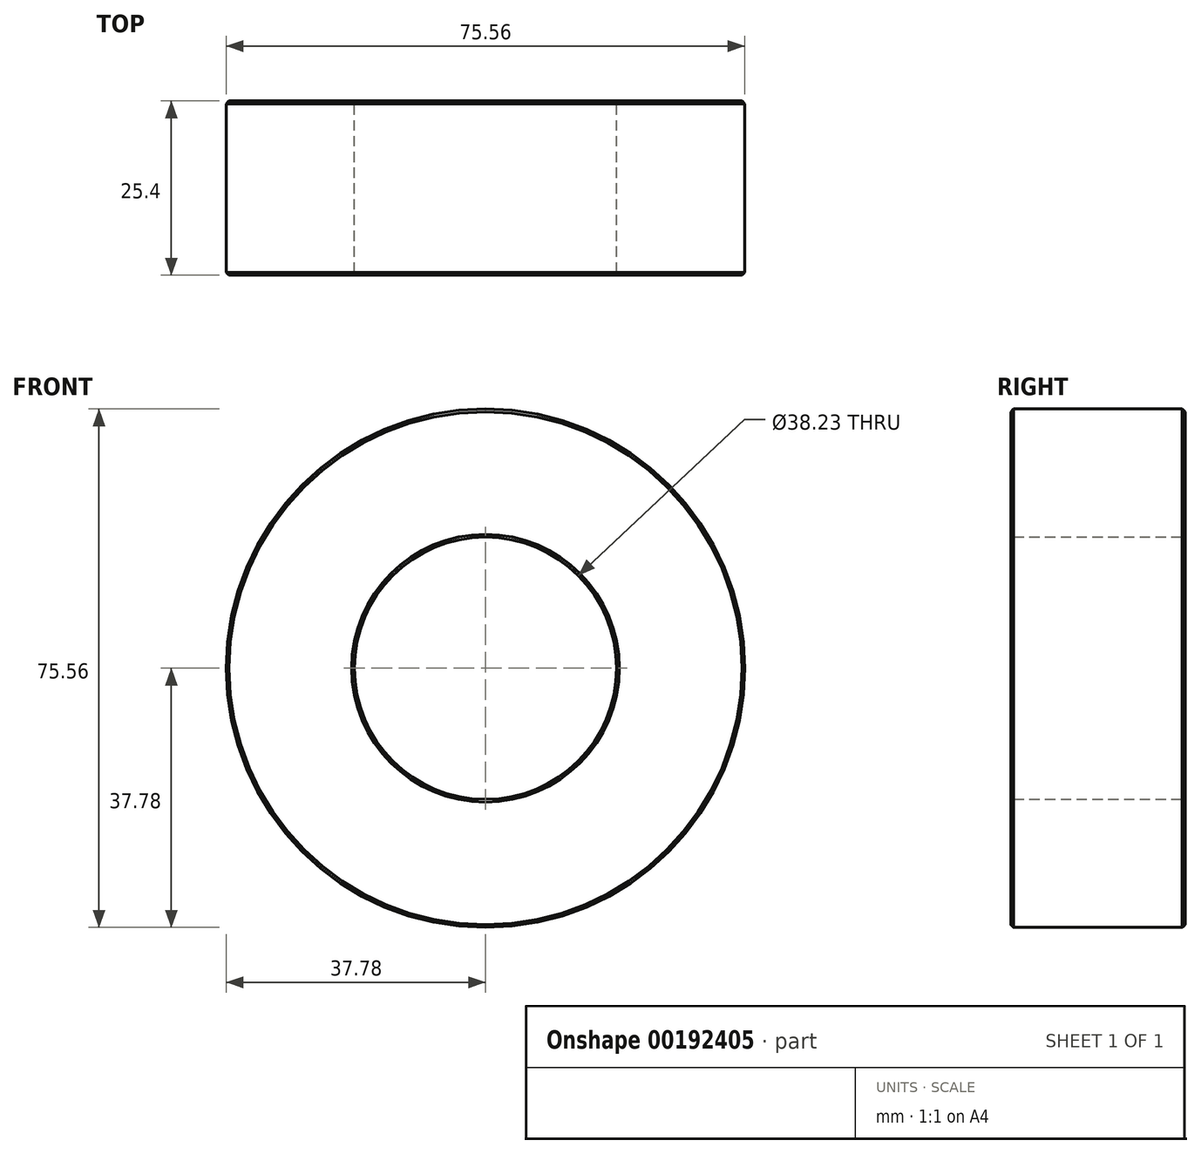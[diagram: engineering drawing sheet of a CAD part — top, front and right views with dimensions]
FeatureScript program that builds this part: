
annotation { "Feature Type Name" : "Feature", "Feature Type Description" : "" }
export const myFeature = defineFeature(function(context is Context, id is Id, definition is map)
    precondition{}
    {
        {
            var Q0;
            Q0=qCreatedBy(makeId("Front.planeOp"),FACE);
            var sketch = newSketch(context, id + "F0", { "sketchPlane" : qUnion([Q0])});
            skCircle(sketch, "E0", {"center": v(0, 0) * mm, "radius": 37.78 * mm});
            skCircle(sketch, "E1", {"center": v(0, 0) * mm, "radius": 19.11 * mm});
            skSolve(sketch);
        }
        {
            var Q0;
            Q0 = qSketchRegion(id + "F0", true);
            extrude(context, id + "F1", {"entities" : qUnion([Q0]), "depth" : 25.4 * mm});
        }
        {
            var Q0;
            Q0=makeQuery(id+"F1.opExtrude","CAP_EDGE",EDGE,{"disambiguationData":[OSD([sQuery(id+"F0.wireOp",EDGE,"E0")])],"isStart":false});
            var Q1;
            Q1=makeQuery(id+"F1.opExtrude","CAP_EDGE",EDGE,{"disambiguationData":[OSD([sQuery(id+"F0.wireOp",EDGE,"E1")])],"isStart":false});
            var Q2;
            Q2=makeQuery(id+"F1.opExtrude","CAP_EDGE",EDGE,{"disambiguationData":[OSD([sQuery(id+"F0.wireOp",EDGE,"E1")])],"isStart":true});
            var Q3;
            Q3=makeQuery(id+"F1.opExtrude","SWEPT_FACE",FACE,{"disambiguationData":[OSD([sQuery(id+"F0.wireOp",EDGE,"E0")])]});
            chamfer(context, id + "F2", {"entities" : qUnion([Q0, Q1, Q2, Q3]), "width" : 0.4 * mm, "tangentPropagation" : true});
        }
    });
